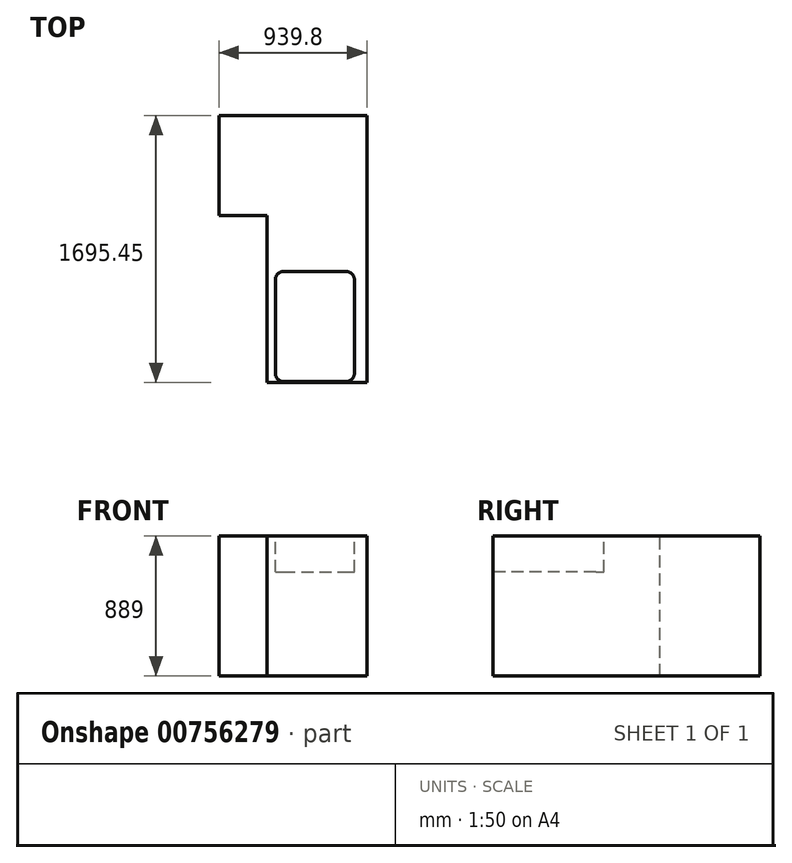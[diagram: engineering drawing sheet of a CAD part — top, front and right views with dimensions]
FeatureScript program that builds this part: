
annotation { "Feature Type Name" : "Feature", "Feature Type Description" : "" }
export const myFeature = defineFeature(function(context is Context, id is Id, definition is map)
    precondition{}
    {
        {
            var Q0;
            Q0=qCreatedBy(makeId("Top.planeOp"),FACE);
            var sketch = newSketch(context, id + "F0", { "sketchPlane" : qUnion([Q0])});
            skLineSegment(sketch, "E0", {"start": v(0, 0) * mm, "end": v(-304.8, 0) * mm});
            skLineSegment(sketch, "E1", {"start": v(0, 0) * mm, "end": v(0, -1060.45) * mm});
            skLineSegment(sketch, "E2", {"start": v(0, -1060.45) * mm, "end": v(635, -1060.45) * mm});
            skLineSegment(sketch, "E3", {"start": v(635, -1060.45) * mm, "end": v(635, 635) * mm});
            skLineSegment(sketch, "E4", {"start": v(635, 635) * mm, "end": v(-304.8, 635) * mm});
            skLineSegment(sketch, "E5", {"start": v(-304.8, 635) * mm, "end": v(-304.8, 0) * mm});
            skSolve(sketch);
        }
        {
            var Q0;
            Q0=makeQuery(id+"F0.imprint","IMPRINT",FACE,{"disambiguationData":[TD([[makeQuery(id+"F0.imprint","IMPRINT",EDGE,{"derivedFrom":sQuery(id+"F0.wireOp",EDGE,"E0")}),-1.0]])]});
            extrude(context, id + "F1", {"entities" : qUnion([Q0]), "oppositeDirection" : true, "depth" : 889 * mm, "offsetDistance" : 25.4 * mm});
        }
        {
            var Q0;
            Q0=makeQuery(id+"F1.opExtrude","CAP_FACE",FACE,{"disambiguationData":[OSD([sQuery(id+"F0.wireOp",EDGE,"E0"),sQuery(id+"F0.wireOp",EDGE,"E1"),sQuery(id+"F0.wireOp",EDGE,"E2"),sQuery(id+"F0.wireOp",EDGE,"E3"),sQuery(id+"F0.wireOp",EDGE,"E4"),sQuery(id+"F0.wireOp",EDGE,"E5")])],"isStart":true});
            var sketch = newSketch(context, id + "F2", { "sketchPlane" : qUnion([Q0])});
            skLineSegment(sketch, "E6.bottom", {"start": v(104.77, -355.6) * mm, "end": v(504.82, -355.6) * mm});
            skLineSegment(sketch, "E6.top", {"start": v(104.77, -1054.1) * mm, "end": v(504.82, -1054.1) * mm});
            skLineSegment(sketch, "E6.left", {"start": v(53.97, -406.4) * mm, "end": v(53.97, -1003.3) * mm});
            skLineSegment(sketch, "E6.right", {"start": v(555.62, -406.4) * mm, "end": v(555.62, -1003.3) * mm});
            skPoint(sketch, "E7.visualSharp", {"position": v(53.97, -355.6) * mm});
            skArc(sketch, "E7.filletArc", {"start": v(104.77, -355.6) * mm, "mid": v(68.85, -370.48) * mm, "end": v(53.97, -406.4) * mm});
            skPoint(sketch, "E8.visualSharp", {"position": v(53.97, -1054.1) * mm});
            skArc(sketch, "E8.filletArc", {"start": v(53.97, -1003.3) * mm, "mid": v(68.85, -1039.22) * mm, "end": v(104.77, -1054.1) * mm});
            skPoint(sketch, "E9.visualSharp", {"position": v(555.62, -1054.1) * mm});
            skArc(sketch, "E9.filletArc", {"start": v(504.82, -1054.1) * mm, "mid": v(540.75, -1039.22) * mm, "end": v(555.62, -1003.3) * mm});
            skPoint(sketch, "E10.visualSharp", {"position": v(555.62, -355.6) * mm});
            skArc(sketch, "E10.filletArc", {"start": v(555.62, -406.4) * mm, "mid": v(540.75, -370.48) * mm, "end": v(504.82, -355.6) * mm});
            skSolve(sketch);
        }
        {
            var Q0;
            Q0=makeQuery(id+"F2.imprint","IMPRINT",FACE,{"disambiguationData":[TD([[makeQuery(id+"F2.imprint","IMPRINT",EDGE,{"derivedFrom":sQuery(id+"F2.wireOp",EDGE,"E6.bottom")}),-1.0]])]});
            extrude(context, id + "F3", {"entities" : qUnion([Q0]), "operationType" : NewBodyOperationType.REMOVE, "oppositeDirection" : true, "depth" : 228.6 * mm, "offsetDistance" : 25.4 * mm});
        }
    });
